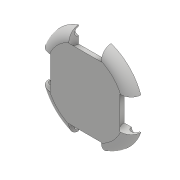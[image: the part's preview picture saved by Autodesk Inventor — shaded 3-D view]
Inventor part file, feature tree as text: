
AUTODESK INVENTOR PART (.ipt)
format: ipt  version: 2017 (Build 210142000, 142)  size: 154,624 bytes
history: native  units: mm
features: sketch x3, extrude x2, revolve x1, fillet x1, pattern_circular x1, projected_geometry x1
ambient origin geometry x8: Origin, YZ Plane, XZ Plane, XY Plane, X Axis, Y Axis, Z Axis, Center Point
bodies: Solid1 (feature_tree)
feature tree (9):
  extrude  "Extrusion1"  Depth=6.0mm TaperAngle=0.0deg
  revolve  "Revolution1"  [1 undecoded]
  extrude  "Extrusion2"  Depth=5.0mm
  fillet  "Fillet1"  Radius=5.0mm
  pattern_circular  "Circular Pattern1"  Angle=90.0deg  [1 undecoded]
  sketch  "Sketch1"  dims[d0=60.0mm d1=6.0mm d2=0.0mm]
  sketch  "Sketch2"  dims[d3=20.0mm d4=25.0mm]
  sketch  "Sketch3"  dims[d5=14.0mm d6=5.0mm d7=5.0mm d8=90.0deg d9=6.0mm d10=0.0mm d11=6.0mm d12=40.0mm d13=360.0deg]
  projected_geometry  "Projected Loop1"
note: 2 required parameter values undecoded (feature->parameter linkage not recoverable at this tier; creation-order binding heuristic only, values carry confidence <= 0.55)